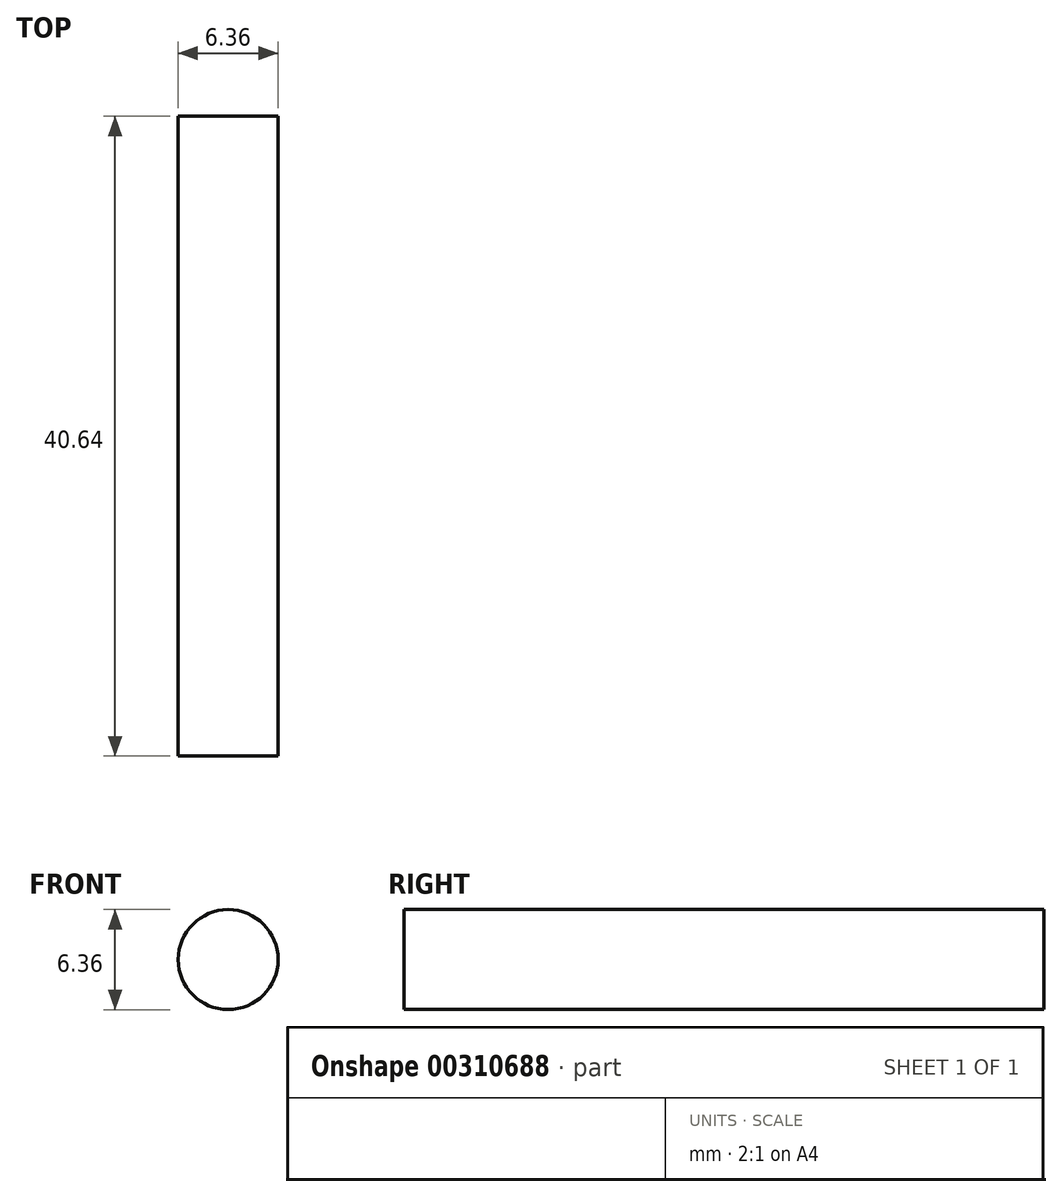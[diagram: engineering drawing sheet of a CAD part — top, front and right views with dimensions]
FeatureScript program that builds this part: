
annotation { "Feature Type Name" : "Feature", "Feature Type Description" : "" }
export const myFeature = defineFeature(function(context is Context, id is Id, definition is map)
    precondition{}
    {
        {
            var Q0;
            Q0=qCreatedBy(makeId("Front.planeOp"),FACE);
            var sketch = newSketch(context, id + "F0", { "sketchPlane" : qUnion([Q0])});
            skCircle(sketch, "E0", {"center": v(0, 0) * mm, "radius": 3.18 * mm});
            skSolve(sketch);
        }
        {
            var Q0;
            Q0=makeQuery(id+"F0.imprint","IMPRINT",FACE,{"disambiguationData":[TD([[makeQuery(id+"F0.imprint","IMPRINT",EDGE,{"derivedFrom":sQuery(id+"F0.wireOp",EDGE,"E0")}),1.0]])]});
            extrude(context, id + "F1", {"entities" : qUnion([Q0]), "depth" : 40.64 * mm});
        }
    });
